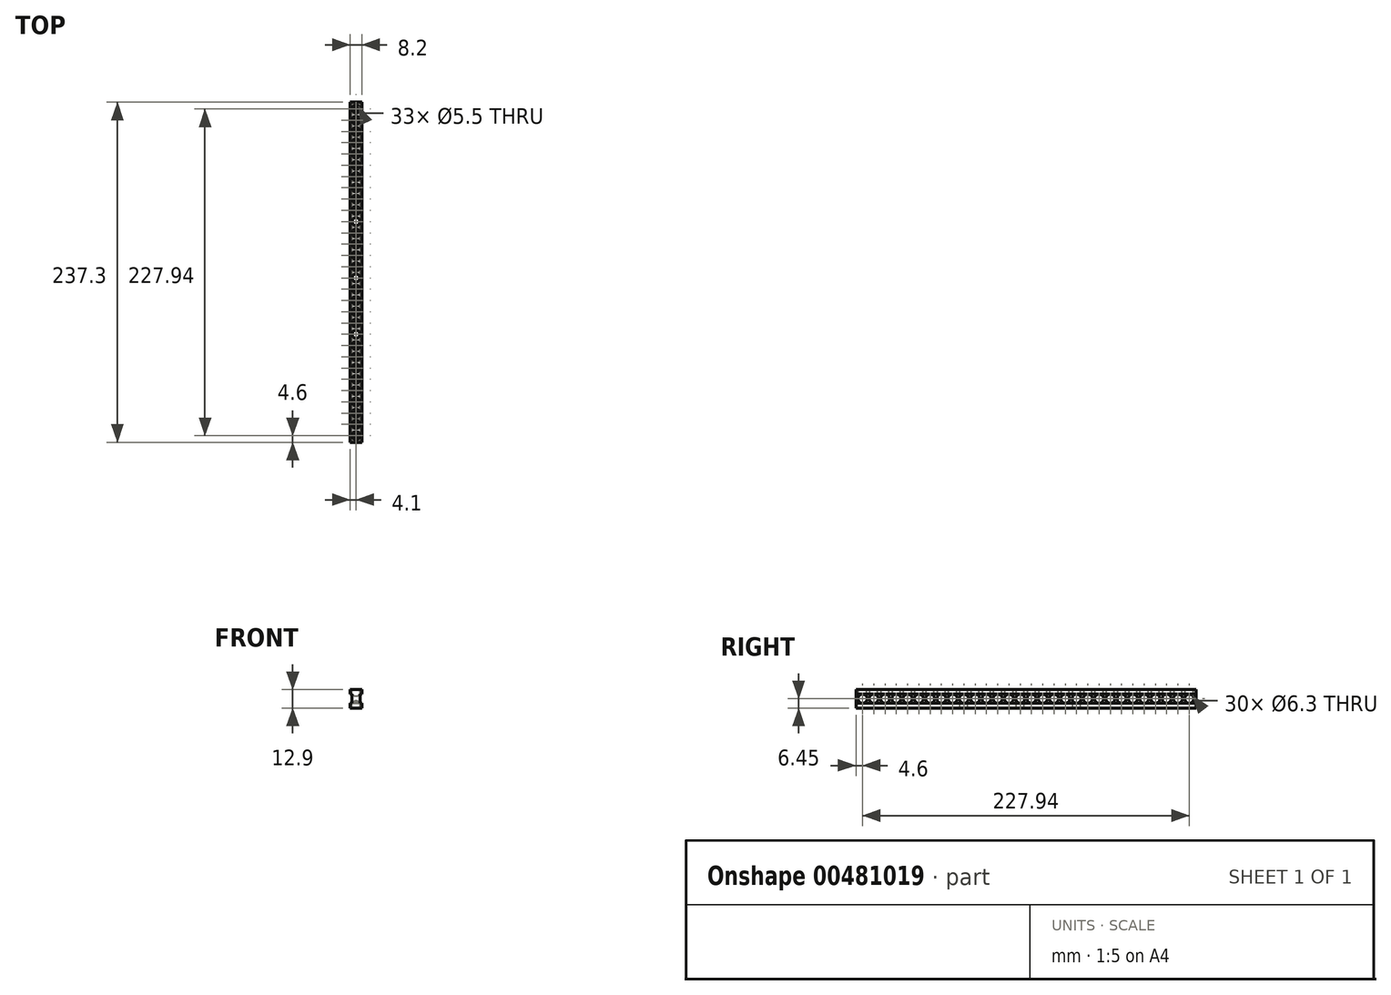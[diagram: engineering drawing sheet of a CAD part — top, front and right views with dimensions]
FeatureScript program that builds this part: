
annotation { "Feature Type Name" : "Feature", "Feature Type Description" : "" }
export const myFeature = defineFeature(function(context is Context, id is Id, definition is map)
    precondition{}
    {
        {
            var Q0;
            Q0=qCreatedBy(makeId("Front.planeOp"),FACE);
            var sketch = newSketch(context, id + "F0", { "sketchPlane" : qUnion([Q0])});
            skLineSegment(sketch, "E0", {"start": v(0, 0) * mm, "end": v(8.2, 0) * mm});
            skLineSegment(sketch, "E1", {"start": v(8.2, 0) * mm, "end": v(8.2, 3.25) * mm});
            skLineSegment(sketch, "E2", {"start": v(8.2, 3.25) * mm, "end": v(6.9, 3.25) * mm});
            skLineSegment(sketch, "E3", {"start": v(6.9, 3.25) * mm, "end": v(6.9, 9.65) * mm});
            skLineSegment(sketch, "E4", {"start": v(6.9, 9.65) * mm, "end": v(8.2, 9.65) * mm});
            skLineSegment(sketch, "E5", {"start": v(8.2, 9.65) * mm, "end": v(8.2, 12.9) * mm});
            skLineSegment(sketch, "E6", {"start": v(8.2, 12.9) * mm, "end": v(0, 12.9) * mm});
            skLineSegment(sketch, "E7", {"start": v(0, 12.9) * mm, "end": v(0, 9.65) * mm});
            skLineSegment(sketch, "E8", {"start": v(0, 9.65) * mm, "end": v(1.3, 9.65) * mm});
            skLineSegment(sketch, "E9", {"start": v(1.3, 9.65) * mm, "end": v(1.3, 3.25) * mm});
            skLineSegment(sketch, "E10", {"start": v(1.3, 3.25) * mm, "end": v(0, 3.25) * mm});
            skLineSegment(sketch, "E11", {"start": v(0, 3.25) * mm, "end": v(0, 0) * mm});
            skSolve(sketch);
        }
        {
            var Q0;
            Q0=makeQuery(id+"F0.imprint","IMPRINT",FACE,{"disambiguationData":[TD([[makeQuery(id+"F0.imprint","IMPRINT",EDGE,{"derivedFrom":sQuery(id+"F0.wireOp",EDGE,"E0")}),1.0]])]});
            extrude(context, id + "F1", {"entities" : qUnion([Q0]), "depth" : 237.3 * mm});
        }
        {
            var Q0;
            Q0=makeQuery(id+"F1.opExtrude","SWEPT_FACE",FACE,{"disambiguationData":[OSD([sQuery(id+"F0.wireOp",EDGE,"E3")])]});
            var sketch = newSketch(context, id + "F2", { "sketchPlane" : qUnion([Q0])});
            skCircle(sketch, "E12", {"center": v(-232.7, 6.45) * mm, "radius": 3.15 * mm});
            skPoint(sketch, "E12.centerSnap0", {"position": v(-237.3, 6.45) * mm});
            skLineSegment(sketch, "E13.direction1", {"start": v(-232.7, 6.45) * mm, "end": v(-224.84, 6.45) * mm, "construction": true});
            skCircle(sketch, "E14.0.1.0", {"center": v(-224.84, 6.45) * mm, "radius": 3.15 * mm});
            skCircle(sketch, "E15.0.2.0", {"center": v(-216.98, 6.45) * mm, "radius": 3.15 * mm});
            skCircle(sketch, "E15.0.3.0", {"center": v(-209.12, 6.45) * mm, "radius": 3.15 * mm});
            skCircle(sketch, "E15.0.4.0", {"center": v(-201.26, 6.45) * mm, "radius": 3.15 * mm});
            skCircle(sketch, "E15.0.5.0", {"center": v(-193.4, 6.45) * mm, "radius": 3.15 * mm});
            skCircle(sketch, "E15.0.6.0", {"center": v(-185.54, 6.45) * mm, "radius": 3.15 * mm});
            skCircle(sketch, "E15.0.7.0", {"center": v(-177.68, 6.45) * mm, "radius": 3.15 * mm});
            skCircle(sketch, "E15.0.8.0", {"center": v(-169.82, 6.45) * mm, "radius": 3.15 * mm});
            skCircle(sketch, "E15.0.9.0", {"center": v(-161.96, 6.45) * mm, "radius": 3.15 * mm});
            skCircle(sketch, "E15.0.10.0", {"center": v(-154.1, 6.45) * mm, "radius": 3.15 * mm});
            skCircle(sketch, "E15.0.11.0", {"center": v(-146.24, 6.45) * mm, "radius": 3.15 * mm});
            skCircle(sketch, "E15.0.12.0", {"center": v(-138.38, 6.45) * mm, "radius": 3.15 * mm});
            skCircle(sketch, "E15.0.13.0", {"center": v(-130.52, 6.45) * mm, "radius": 3.15 * mm});
            skCircle(sketch, "E15.0.14.0", {"center": v(-122.66, 6.45) * mm, "radius": 3.15 * mm});
            skCircle(sketch, "E15.0.15.0", {"center": v(-114.8, 6.45) * mm, "radius": 3.15 * mm});
            skCircle(sketch, "E15.0.16.0", {"center": v(-106.94, 6.45) * mm, "radius": 3.15 * mm});
            skCircle(sketch, "E15.0.17.0", {"center": v(-99.08, 6.45) * mm, "radius": 3.15 * mm});
            skCircle(sketch, "E15.0.18.0", {"center": v(-91.22, 6.45) * mm, "radius": 3.15 * mm});
            skCircle(sketch, "E15.0.19.0", {"center": v(-83.36, 6.45) * mm, "radius": 3.15 * mm});
            skCircle(sketch, "E15.0.20.0", {"center": v(-75.5, 6.45) * mm, "radius": 3.15 * mm});
            skCircle(sketch, "E15.0.21.0", {"center": v(-67.64, 6.45) * mm, "radius": 3.15 * mm});
            skCircle(sketch, "E15.0.22.0", {"center": v(-59.78, 6.45) * mm, "radius": 3.15 * mm});
            skCircle(sketch, "E15.0.23.0", {"center": v(-51.92, 6.45) * mm, "radius": 3.15 * mm});
            skCircle(sketch, "E15.0.24.0", {"center": v(-44.06, 6.45) * mm, "radius": 3.15 * mm});
            skCircle(sketch, "E15.0.25.0", {"center": v(-36.2, 6.45) * mm, "radius": 3.15 * mm});
            skCircle(sketch, "E15.0.26.0", {"center": v(-28.34, 6.45) * mm, "radius": 3.15 * mm});
            skCircle(sketch, "E15.0.27.0", {"center": v(-20.48, 6.45) * mm, "radius": 3.15 * mm});
            skCircle(sketch, "E15.0.28.0", {"center": v(-12.62, 6.45) * mm, "radius": 3.15 * mm});
            skCircle(sketch, "E15.0.29.0", {"center": v(-4.76, 6.45) * mm, "radius": 3.15 * mm});
            skSolve(sketch);
        }
        {
            var Q0;
            Q0=makeQuery(id+"F2.imprint","IMPRINT",FACE,{"disambiguationData":[TD([[makeQuery(id+"F2.imprint","IMPRINT",EDGE,{"derivedFrom":sQuery(id+"F2.wireOp",EDGE,"E12")}),1.0]])]});
            var Q1;
            Q1=makeQuery(id+"F2.imprint","IMPRINT",FACE,{"disambiguationData":[TD([[makeQuery(id+"F2.imprint","IMPRINT",EDGE,{"derivedFrom":sQuery(id+"F2.wireOp",EDGE,"E13.1.0.0")}),1.0]])]});
            var Q2;
            Q2=makeQuery(id+"F2.imprint","IMPRINT",FACE,{"disambiguationData":[TD([[makeQuery(id+"F2.imprint","IMPRINT",EDGE,{"derivedFrom":sQuery(id+"F2.wireOp",EDGE,"E13.2.0.0")}),1.0]])]});
            var Q3;
            Q3=makeQuery(id+"F2.imprint","IMPRINT",FACE,{"disambiguationData":[TD([[makeQuery(id+"F2.imprint","IMPRINT",EDGE,{"derivedFrom":sQuery(id+"F2.wireOp",EDGE,"E13.3.0.0")}),1.0]])]});
            var Q4;
            Q4=makeQuery(id+"F2.imprint","IMPRINT",FACE,{"disambiguationData":[TD([[makeQuery(id+"F2.imprint","IMPRINT",EDGE,{"derivedFrom":sQuery(id+"F2.wireOp",EDGE,"E13.4.0.0")}),1.0]])]});
            var Q5;
            Q5=makeQuery(id+"F2.imprint","IMPRINT",FACE,{"disambiguationData":[TD([[makeQuery(id+"F2.imprint","IMPRINT",EDGE,{"derivedFrom":sQuery(id+"F2.wireOp",EDGE,"E13.5.0.0")}),1.0]])]});
            var Q6;
            Q6=makeQuery(id+"F2.imprint","IMPRINT",FACE,{"disambiguationData":[TD([[makeQuery(id+"F2.imprint","IMPRINT",EDGE,{"derivedFrom":sQuery(id+"F2.wireOp",EDGE,"E13.6.0.0")}),1.0]])]});
            var Q7;
            Q7=makeQuery(id+"F2.imprint","IMPRINT",FACE,{"disambiguationData":[TD([[makeQuery(id+"F2.imprint","IMPRINT",EDGE,{"derivedFrom":sQuery(id+"F2.wireOp",EDGE,"E13.7.0.0")}),1.0]])]});
            var Q8;
            Q8=makeQuery(id+"F2.imprint","IMPRINT",FACE,{"disambiguationData":[TD([[makeQuery(id+"F2.imprint","IMPRINT",EDGE,{"derivedFrom":sQuery(id+"F2.wireOp",EDGE,"E13.8.0.0")}),1.0]])]});
            var Q9;
            Q9=makeQuery(id+"F2.imprint","IMPRINT",FACE,{"disambiguationData":[TD([[makeQuery(id+"F2.imprint","IMPRINT",EDGE,{"derivedFrom":sQuery(id+"F2.wireOp",EDGE,"E13.9.0.0")}),1.0]])]});
            var Q10;
            Q10=makeQuery(id+"F2.imprint","IMPRINT",FACE,{"disambiguationData":[TD([[makeQuery(id+"F2.imprint","IMPRINT",EDGE,{"derivedFrom":sQuery(id+"F2.wireOp",EDGE,"E13.10.0.0")}),1.0]])]});
            var Q11;
            Q11=makeQuery(id+"F2.imprint","IMPRINT",FACE,{"disambiguationData":[TD([[makeQuery(id+"F2.imprint","IMPRINT",EDGE,{"derivedFrom":sQuery(id+"F2.wireOp",EDGE,"E13.11.0.0")}),1.0]])]});
            var Q12;
            Q12=makeQuery(id+"F2.imprint","IMPRINT",FACE,{"disambiguationData":[TD([[makeQuery(id+"F2.imprint","IMPRINT",EDGE,{"derivedFrom":sQuery(id+"F2.wireOp",EDGE,"E13.12.0.0")}),1.0]])]});
            var Q13;
            Q13=makeQuery(id+"F2.imprint","IMPRINT",FACE,{"disambiguationData":[TD([[makeQuery(id+"F2.imprint","IMPRINT",EDGE,{"derivedFrom":sQuery(id+"F2.wireOp",EDGE,"E13.13.0.0")}),1.0]])]});
            var Q14;
            Q14=makeQuery(id+"F2.imprint","IMPRINT",FACE,{"disambiguationData":[TD([[makeQuery(id+"F2.imprint","IMPRINT",EDGE,{"derivedFrom":sQuery(id+"F2.wireOp",EDGE,"E13.14.0.0")}),1.0]])]});
            var Q15;
            Q15=makeQuery(id+"F2.imprint","IMPRINT",FACE,{"disambiguationData":[TD([[makeQuery(id+"F2.imprint","IMPRINT",EDGE,{"derivedFrom":sQuery(id+"F2.wireOp",EDGE,"E13.15.0.0")}),1.0]])]});
            var Q16;
            Q16=makeQuery(id+"F2.imprint","IMPRINT",FACE,{"disambiguationData":[TD([[makeQuery(id+"F2.imprint","IMPRINT",EDGE,{"derivedFrom":sQuery(id+"F2.wireOp",EDGE,"E13.16.0.0")}),1.0]])]});
            var Q17;
            Q17=makeQuery(id+"F2.imprint","IMPRINT",FACE,{"disambiguationData":[TD([[makeQuery(id+"F2.imprint","IMPRINT",EDGE,{"derivedFrom":sQuery(id+"F2.wireOp",EDGE,"E13.17.0.0")}),1.0]])]});
            var Q18;
            Q18=makeQuery(id+"F2.imprint","IMPRINT",FACE,{"disambiguationData":[TD([[makeQuery(id+"F2.imprint","IMPRINT",EDGE,{"derivedFrom":sQuery(id+"F2.wireOp",EDGE,"E13.18.0.0")}),1.0]])]});
            var Q19;
            Q19=makeQuery(id+"F2.imprint","IMPRINT",FACE,{"disambiguationData":[TD([[makeQuery(id+"F2.imprint","IMPRINT",EDGE,{"derivedFrom":sQuery(id+"F2.wireOp",EDGE,"E13.19.0.0")}),1.0]])]});
            var Q20;
            Q20=makeQuery(id+"F2.imprint","IMPRINT",FACE,{"disambiguationData":[TD([[makeQuery(id+"F2.imprint","IMPRINT",EDGE,{"derivedFrom":sQuery(id+"F2.wireOp",EDGE,"E13.20.0.0")}),1.0]])]});
            var Q21;
            Q21=makeQuery(id+"F2.imprint","IMPRINT",FACE,{"disambiguationData":[TD([[makeQuery(id+"F2.imprint","IMPRINT",EDGE,{"derivedFrom":sQuery(id+"F2.wireOp",EDGE,"E13.21.0.0")}),1.0]])]});
            var Q22;
            Q22=makeQuery(id+"F2.imprint","IMPRINT",FACE,{"disambiguationData":[TD([[makeQuery(id+"F2.imprint","IMPRINT",EDGE,{"derivedFrom":sQuery(id+"F2.wireOp",EDGE,"E13.22.0.0")}),1.0]])]});
            var Q23;
            Q23=makeQuery(id+"F2.imprint","IMPRINT",FACE,{"disambiguationData":[TD([[makeQuery(id+"F2.imprint","IMPRINT",EDGE,{"derivedFrom":sQuery(id+"F2.wireOp",EDGE,"E13.23.0.0")}),1.0]])]});
            var Q24;
            Q24=makeQuery(id+"F2.imprint","IMPRINT",FACE,{"disambiguationData":[TD([[makeQuery(id+"F2.imprint","IMPRINT",EDGE,{"derivedFrom":sQuery(id+"F2.wireOp",EDGE,"E13.24.0.0")}),1.0]])]});
            var Q25;
            Q25=makeQuery(id+"F2.imprint","IMPRINT",FACE,{"disambiguationData":[TD([[makeQuery(id+"F2.imprint","IMPRINT",EDGE,{"derivedFrom":sQuery(id+"F2.wireOp",EDGE,"E13.25.0.0")}),1.0]])]});
            var Q26;
            Q26=makeQuery(id+"F2.imprint","IMPRINT",FACE,{"disambiguationData":[TD([[makeQuery(id+"F2.imprint","IMPRINT",EDGE,{"derivedFrom":sQuery(id+"F2.wireOp",EDGE,"E13.26.0.0")}),1.0]])]});
            var Q27;
            Q27=makeQuery(id+"F2.imprint","IMPRINT",FACE,{"disambiguationData":[TD([[makeQuery(id+"F2.imprint","IMPRINT",EDGE,{"derivedFrom":sQuery(id+"F2.wireOp",EDGE,"E13.27.0.0")}),1.0]])]});
            var Q28;
            Q28=makeQuery(id+"F2.imprint","IMPRINT",FACE,{"disambiguationData":[TD([[makeQuery(id+"F2.imprint","IMPRINT",EDGE,{"derivedFrom":sQuery(id+"F2.wireOp",EDGE,"E13.28.0.0")}),1.0]])]});
            var Q29;
            Q29=makeQuery(id+"F2.imprint","IMPRINT",FACE,{"disambiguationData":[TD([[makeQuery(id+"F2.imprint","IMPRINT",EDGE,{"derivedFrom":sQuery(id+"F2.wireOp",EDGE,"E14.0.1.0")}),1.0]])]});
            var Q30;
            Q30=makeQuery(id+"F2.imprint","IMPRINT",FACE,{"disambiguationData":[TD([[makeQuery(id+"F2.imprint","IMPRINT",EDGE,{"derivedFrom":sQuery(id+"F2.wireOp",EDGE,"E15.0.2.0")}),1.0]])]});
            var Q31;
            Q31=makeQuery(id+"F2.imprint","IMPRINT",FACE,{"disambiguationData":[TD([[makeQuery(id+"F2.imprint","IMPRINT",EDGE,{"derivedFrom":sQuery(id+"F2.wireOp",EDGE,"E15.0.3.0")}),1.0]])]});
            var Q32;
            Q32=makeQuery(id+"F2.imprint","IMPRINT",FACE,{"disambiguationData":[TD([[makeQuery(id+"F2.imprint","IMPRINT",EDGE,{"derivedFrom":sQuery(id+"F2.wireOp",EDGE,"E15.0.4.0")}),1.0]])]});
            var Q33;
            Q33=makeQuery(id+"F2.imprint","IMPRINT",FACE,{"disambiguationData":[TD([[makeQuery(id+"F2.imprint","IMPRINT",EDGE,{"derivedFrom":sQuery(id+"F2.wireOp",EDGE,"E15.0.5.0")}),1.0]])]});
            var Q34;
            Q34=makeQuery(id+"F2.imprint","IMPRINT",FACE,{"disambiguationData":[TD([[makeQuery(id+"F2.imprint","IMPRINT",EDGE,{"derivedFrom":sQuery(id+"F2.wireOp",EDGE,"E15.0.6.0")}),1.0]])]});
            var Q35;
            Q35=makeQuery(id+"F2.imprint","IMPRINT",FACE,{"disambiguationData":[TD([[makeQuery(id+"F2.imprint","IMPRINT",EDGE,{"derivedFrom":sQuery(id+"F2.wireOp",EDGE,"E15.0.7.0")}),1.0]])]});
            var Q36;
            Q36=makeQuery(id+"F2.imprint","IMPRINT",FACE,{"disambiguationData":[TD([[makeQuery(id+"F2.imprint","IMPRINT",EDGE,{"derivedFrom":sQuery(id+"F2.wireOp",EDGE,"E15.0.8.0")}),1.0]])]});
            var Q37;
            Q37=makeQuery(id+"F2.imprint","IMPRINT",FACE,{"disambiguationData":[TD([[makeQuery(id+"F2.imprint","IMPRINT",EDGE,{"derivedFrom":sQuery(id+"F2.wireOp",EDGE,"E15.0.9.0")}),1.0]])]});
            var Q38;
            Q38=makeQuery(id+"F2.imprint","IMPRINT",FACE,{"disambiguationData":[TD([[makeQuery(id+"F2.imprint","IMPRINT",EDGE,{"derivedFrom":sQuery(id+"F2.wireOp",EDGE,"E15.0.10.0")}),1.0]])]});
            var Q39;
            Q39=makeQuery(id+"F2.imprint","IMPRINT",FACE,{"disambiguationData":[TD([[makeQuery(id+"F2.imprint","IMPRINT",EDGE,{"derivedFrom":sQuery(id+"F2.wireOp",EDGE,"E15.0.11.0")}),1.0]])]});
            var Q40;
            Q40=makeQuery(id+"F2.imprint","IMPRINT",FACE,{"disambiguationData":[TD([[makeQuery(id+"F2.imprint","IMPRINT",EDGE,{"derivedFrom":sQuery(id+"F2.wireOp",EDGE,"E15.0.12.0")}),1.0]])]});
            var Q41;
            Q41=makeQuery(id+"F2.imprint","IMPRINT",FACE,{"disambiguationData":[TD([[makeQuery(id+"F2.imprint","IMPRINT",EDGE,{"derivedFrom":sQuery(id+"F2.wireOp",EDGE,"E15.0.13.0")}),1.0]])]});
            var Q42;
            Q42=makeQuery(id+"F2.imprint","IMPRINT",FACE,{"disambiguationData":[TD([[makeQuery(id+"F2.imprint","IMPRINT",EDGE,{"derivedFrom":sQuery(id+"F2.wireOp",EDGE,"E15.0.14.0")}),1.0]])]});
            var Q43;
            Q43=makeQuery(id+"F2.imprint","IMPRINT",FACE,{"disambiguationData":[TD([[makeQuery(id+"F2.imprint","IMPRINT",EDGE,{"derivedFrom":sQuery(id+"F2.wireOp",EDGE,"E15.0.15.0")}),1.0]])]});
            var Q44;
            Q44=makeQuery(id+"F2.imprint","IMPRINT",FACE,{"disambiguationData":[TD([[makeQuery(id+"F2.imprint","IMPRINT",EDGE,{"derivedFrom":sQuery(id+"F2.wireOp",EDGE,"E15.0.16.0")}),1.0]])]});
            var Q45;
            Q45=makeQuery(id+"F2.imprint","IMPRINT",FACE,{"disambiguationData":[TD([[makeQuery(id+"F2.imprint","IMPRINT",EDGE,{"derivedFrom":sQuery(id+"F2.wireOp",EDGE,"E15.0.17.0")}),1.0]])]});
            var Q46;
            Q46=makeQuery(id+"F2.imprint","IMPRINT",FACE,{"disambiguationData":[TD([[makeQuery(id+"F2.imprint","IMPRINT",EDGE,{"derivedFrom":sQuery(id+"F2.wireOp",EDGE,"E15.0.18.0")}),1.0]])]});
            var Q47;
            Q47=makeQuery(id+"F2.imprint","IMPRINT",FACE,{"disambiguationData":[TD([[makeQuery(id+"F2.imprint","IMPRINT",EDGE,{"derivedFrom":sQuery(id+"F2.wireOp",EDGE,"E15.0.19.0")}),1.0]])]});
            var Q48;
            Q48=makeQuery(id+"F2.imprint","IMPRINT",FACE,{"disambiguationData":[TD([[makeQuery(id+"F2.imprint","IMPRINT",EDGE,{"derivedFrom":sQuery(id+"F2.wireOp",EDGE,"E15.0.20.0")}),1.0]])]});
            var Q49;
            Q49=makeQuery(id+"F2.imprint","IMPRINT",FACE,{"disambiguationData":[TD([[makeQuery(id+"F2.imprint","IMPRINT",EDGE,{"derivedFrom":sQuery(id+"F2.wireOp",EDGE,"E15.0.21.0")}),1.0]])]});
            var Q50;
            Q50=makeQuery(id+"F2.imprint","IMPRINT",FACE,{"disambiguationData":[TD([[makeQuery(id+"F2.imprint","IMPRINT",EDGE,{"derivedFrom":sQuery(id+"F2.wireOp",EDGE,"E15.0.22.0")}),1.0]])]});
            var Q51;
            Q51=makeQuery(id+"F2.imprint","IMPRINT",FACE,{"disambiguationData":[TD([[makeQuery(id+"F2.imprint","IMPRINT",EDGE,{"derivedFrom":sQuery(id+"F2.wireOp",EDGE,"E15.0.23.0")}),1.0]])]});
            var Q52;
            Q52=makeQuery(id+"F2.imprint","IMPRINT",FACE,{"disambiguationData":[TD([[makeQuery(id+"F2.imprint","IMPRINT",EDGE,{"derivedFrom":sQuery(id+"F2.wireOp",EDGE,"E15.0.24.0")}),1.0]])]});
            var Q53;
            Q53=makeQuery(id+"F2.imprint","IMPRINT",FACE,{"disambiguationData":[TD([[makeQuery(id+"F2.imprint","IMPRINT",EDGE,{"derivedFrom":sQuery(id+"F2.wireOp",EDGE,"E15.0.25.0")}),1.0]])]});
            var Q54;
            Q54=makeQuery(id+"F2.imprint","IMPRINT",FACE,{"disambiguationData":[TD([[makeQuery(id+"F2.imprint","IMPRINT",EDGE,{"derivedFrom":sQuery(id+"F2.wireOp",EDGE,"E15.0.26.0")}),1.0]])]});
            var Q55;
            Q55=makeQuery(id+"F2.imprint","IMPRINT",FACE,{"disambiguationData":[TD([[makeQuery(id+"F2.imprint","IMPRINT",EDGE,{"derivedFrom":sQuery(id+"F2.wireOp",EDGE,"E15.0.27.0")}),1.0]])]});
            var Q56;
            Q56=makeQuery(id+"F2.imprint","IMPRINT",FACE,{"disambiguationData":[TD([[makeQuery(id+"F2.imprint","IMPRINT",EDGE,{"derivedFrom":sQuery(id+"F2.wireOp",EDGE,"E15.0.28.0")}),1.0]])]});
            var Q57;
            Q57=makeQuery(id+"F2.imprint","IMPRINT",FACE,{"disambiguationData":[TD([[makeQuery(id+"F2.imprint","IMPRINT",EDGE,{"derivedFrom":sQuery(id+"F2.wireOp",EDGE,"E15.0.29.0")}),1.0]])]});
            var Q58;
            Q58=sQuery(id+"F2.wireOp",EDGE,"E12");
            extrude(context, id + "F3", {"entities" : qUnion([Q0, Q1, Q2, Q3, Q4, Q5, Q6, Q7, Q8, Q9, Q10, Q11, Q12, Q13, Q14, Q15, Q16, Q17, Q18, Q19, Q20, Q21, Q22, Q23, Q24, Q25, Q26, Q27, Q28, Q29, Q30, Q31, Q32, Q33, Q34, Q35, Q36, Q37, Q38, Q39, Q40, Q41, Q42, Q43, Q44, Q45, Q46, Q47, Q48, Q49, Q50, Q51, Q52, Q53, Q54, Q55, Q56, Q57]), "operationType" : NewBodyOperationType.REMOVE, "surfaceEntities" : qUnion([Q58]), "endBound" : BoundingType.THROUGH_ALL, "oppositeDirection" : true, "depth" : 25 * mm});
        }
        {
            var Q0;
            Q0=makeQuery(id+"F1.opExtrude","SWEPT_FACE",FACE,{"disambiguationData":[OSD([sQuery(id+"F0.wireOp",EDGE,"E6")])]});
            var sketch = newSketch(context, id + "F4", { "sketchPlane" : qUnion([Q0])});
            skCircle(sketch, "E16", {"center": v(4.1, -232.7) * mm, "radius": 2.75 * mm});
            skPoint(sketch, "E16.centerSnap0", {"position": v(4.1, -237.3) * mm});
            skCircle(sketch, "E17.0.1.0", {"center": v(4.1, -224.84) * mm, "radius": 2.75 * mm});
            skCircle(sketch, "E17.0.2.0", {"center": v(4.1, -216.98) * mm, "radius": 2.75 * mm});
            skCircle(sketch, "E17.0.3.0", {"center": v(4.1, -209.12) * mm, "radius": 2.75 * mm});
            skCircle(sketch, "E17.0.4.0", {"center": v(4.1, -201.26) * mm, "radius": 2.75 * mm});
            skCircle(sketch, "E17.0.5.0", {"center": v(4.1, -193.4) * mm, "radius": 2.75 * mm});
            skCircle(sketch, "E17.0.6.0", {"center": v(4.1, -185.54) * mm, "radius": 2.75 * mm});
            skCircle(sketch, "E17.0.7.0", {"center": v(4.1, -177.68) * mm, "radius": 2.75 * mm});
            skCircle(sketch, "E17.0.8.0", {"center": v(4.1, -169.82) * mm, "radius": 2.75 * mm});
            skCircle(sketch, "E17.0.9.0", {"center": v(4.1, -161.96) * mm, "radius": 2.75 * mm});
            skCircle(sketch, "E17.0.10.0", {"center": v(4.1, -154.1) * mm, "radius": 2.75 * mm});
            skCircle(sketch, "E17.0.11.0", {"center": v(4.1, -146.24) * mm, "radius": 2.75 * mm});
            skCircle(sketch, "E17.0.12.0", {"center": v(4.1, -138.38) * mm, "radius": 2.75 * mm});
            skCircle(sketch, "E17.0.13.0", {"center": v(4.1, -130.52) * mm, "radius": 2.75 * mm});
            skCircle(sketch, "E17.0.14.0", {"center": v(4.1, -122.66) * mm, "radius": 2.75 * mm});
            skCircle(sketch, "E17.0.15.0", {"center": v(4.1, -114.8) * mm, "radius": 2.75 * mm});
            skCircle(sketch, "E17.0.16.0", {"center": v(4.1, -106.94) * mm, "radius": 2.75 * mm});
            skCircle(sketch, "E17.0.17.0", {"center": v(4.1, -99.08) * mm, "radius": 2.75 * mm});
            skCircle(sketch, "E17.0.18.0", {"center": v(4.1, -91.22) * mm, "radius": 2.75 * mm});
            skCircle(sketch, "E17.0.19.0", {"center": v(4.1, -83.36) * mm, "radius": 2.75 * mm});
            skCircle(sketch, "E17.0.20.0", {"center": v(4.1, -75.5) * mm, "radius": 2.75 * mm});
            skCircle(sketch, "E17.0.21.0", {"center": v(4.1, -67.64) * mm, "radius": 2.75 * mm});
            skCircle(sketch, "E17.0.22.0", {"center": v(4.1, -59.78) * mm, "radius": 2.75 * mm});
            skCircle(sketch, "E17.0.23.0", {"center": v(4.1, -51.92) * mm, "radius": 2.75 * mm});
            skCircle(sketch, "E17.0.24.0", {"center": v(4.1, -44.06) * mm, "radius": 2.75 * mm});
            skCircle(sketch, "E17.0.25.0", {"center": v(4.1, -36.2) * mm, "radius": 2.75 * mm});
            skCircle(sketch, "E17.0.26.0", {"center": v(4.1, -28.34) * mm, "radius": 2.75 * mm});
            skCircle(sketch, "E17.0.27.0", {"center": v(4.1, -20.48) * mm, "radius": 2.75 * mm});
            skCircle(sketch, "E17.0.28.0", {"center": v(4.1, -12.62) * mm, "radius": 2.75 * mm});
            skLineSegment(sketch, "E17.direction1", {"start": v(4.1, -232.7) * mm, "end": v(29.1, -232.7) * mm, "construction": true});
            skLineSegment(sketch, "E17.direction2", {"start": v(4.1, -232.7) * mm, "end": v(4.1, -224.84) * mm, "construction": true});
            skCircle(sketch, "E18.0.0.29", {"center": v(4.1, -4.76) * mm, "radius": 2.75 * mm});
            skSolve(sketch);
        }
        {
            var Q0;
            Q0=makeQuery(id+"F4.imprint","IMPRINT",FACE,{"disambiguationData":[TD([[makeQuery(id+"F4.imprint","IMPRINT",EDGE,{"derivedFrom":sQuery(id+"F4.wireOp",EDGE,"E16")}),1.0]])]});
            var Q1;
            Q1=makeQuery(id+"F4.imprint","IMPRINT",FACE,{"disambiguationData":[TD([[makeQuery(id+"F4.imprint","IMPRINT",EDGE,{"derivedFrom":sQuery(id+"F4.wireOp",EDGE,"E17.0.1.0")}),1.0]])]});
            var Q2;
            Q2=makeQuery(id+"F4.imprint","IMPRINT",FACE,{"disambiguationData":[TD([[makeQuery(id+"F4.imprint","IMPRINT",EDGE,{"derivedFrom":sQuery(id+"F4.wireOp",EDGE,"E17.0.2.0")}),1.0]])]});
            var Q3;
            Q3=makeQuery(id+"F4.imprint","IMPRINT",FACE,{"disambiguationData":[TD([[makeQuery(id+"F4.imprint","IMPRINT",EDGE,{"derivedFrom":sQuery(id+"F4.wireOp",EDGE,"E17.0.3.0")}),1.0]])]});
            var Q4;
            Q4=makeQuery(id+"F4.imprint","IMPRINT",FACE,{"disambiguationData":[TD([[makeQuery(id+"F4.imprint","IMPRINT",EDGE,{"derivedFrom":sQuery(id+"F4.wireOp",EDGE,"E17.0.4.0")}),1.0]])]});
            var Q5;
            Q5=makeQuery(id+"F4.imprint","IMPRINT",FACE,{"disambiguationData":[TD([[makeQuery(id+"F4.imprint","IMPRINT",EDGE,{"derivedFrom":sQuery(id+"F4.wireOp",EDGE,"E17.0.5.0")}),1.0]])]});
            var Q6;
            Q6=makeQuery(id+"F4.imprint","IMPRINT",FACE,{"disambiguationData":[TD([[makeQuery(id+"F4.imprint","IMPRINT",EDGE,{"derivedFrom":sQuery(id+"F4.wireOp",EDGE,"E17.0.6.0")}),1.0]])]});
            var Q7;
            Q7=makeQuery(id+"F4.imprint","IMPRINT",FACE,{"disambiguationData":[TD([[makeQuery(id+"F4.imprint","IMPRINT",EDGE,{"derivedFrom":sQuery(id+"F4.wireOp",EDGE,"E17.0.7.0")}),1.0]])]});
            var Q8;
            Q8=makeQuery(id+"F4.imprint","IMPRINT",FACE,{"disambiguationData":[TD([[makeQuery(id+"F4.imprint","IMPRINT",EDGE,{"derivedFrom":sQuery(id+"F4.wireOp",EDGE,"E17.0.8.0")}),1.0]])]});
            var Q9;
            Q9=makeQuery(id+"F4.imprint","IMPRINT",FACE,{"disambiguationData":[TD([[makeQuery(id+"F4.imprint","IMPRINT",EDGE,{"derivedFrom":sQuery(id+"F4.wireOp",EDGE,"E17.0.10.0")}),1.0]])]});
            var Q10;
            Q10=makeQuery(id+"F4.imprint","IMPRINT",FACE,{"disambiguationData":[TD([[makeQuery(id+"F4.imprint","IMPRINT",EDGE,{"derivedFrom":sQuery(id+"F4.wireOp",EDGE,"E17.0.11.0")}),1.0]])]});
            var Q11;
            Q11=makeQuery(id+"F4.imprint","IMPRINT",FACE,{"disambiguationData":[TD([[makeQuery(id+"F4.imprint","IMPRINT",EDGE,{"derivedFrom":sQuery(id+"F4.wireOp",EDGE,"E17.0.12.0")}),1.0]])]});
            var Q12;
            Q12=makeQuery(id+"F4.imprint","IMPRINT",FACE,{"disambiguationData":[TD([[makeQuery(id+"F4.imprint","IMPRINT",EDGE,{"derivedFrom":sQuery(id+"F4.wireOp",EDGE,"E17.0.13.0")}),1.0]])]});
            var Q13;
            Q13=makeQuery(id+"F4.imprint","IMPRINT",FACE,{"disambiguationData":[TD([[makeQuery(id+"F4.imprint","IMPRINT",EDGE,{"derivedFrom":sQuery(id+"F4.wireOp",EDGE,"E17.0.15.0")}),1.0]])]});
            var Q14;
            Q14=makeQuery(id+"F4.imprint","IMPRINT",FACE,{"disambiguationData":[TD([[makeQuery(id+"F4.imprint","IMPRINT",EDGE,{"derivedFrom":sQuery(id+"F4.wireOp",EDGE,"E17.0.16.0")}),1.0]])]});
            var Q15;
            Q15=makeQuery(id+"F4.imprint","IMPRINT",FACE,{"disambiguationData":[TD([[makeQuery(id+"F4.imprint","IMPRINT",EDGE,{"derivedFrom":sQuery(id+"F4.wireOp",EDGE,"E17.0.17.0")}),1.0]])]});
            var Q16;
            Q16=makeQuery(id+"F4.imprint","IMPRINT",FACE,{"disambiguationData":[TD([[makeQuery(id+"F4.imprint","IMPRINT",EDGE,{"derivedFrom":sQuery(id+"F4.wireOp",EDGE,"E17.0.18.0")}),1.0]])]});
            var Q17;
            Q17=makeQuery(id+"F4.imprint","IMPRINT",FACE,{"disambiguationData":[TD([[makeQuery(id+"F4.imprint","IMPRINT",EDGE,{"derivedFrom":sQuery(id+"F4.wireOp",EDGE,"E17.0.20.0")}),1.0]])]});
            var Q18;
            Q18=makeQuery(id+"F4.imprint","IMPRINT",FACE,{"disambiguationData":[TD([[makeQuery(id+"F4.imprint","IMPRINT",EDGE,{"derivedFrom":sQuery(id+"F4.wireOp",EDGE,"E17.0.21.0")}),1.0]])]});
            var Q19;
            Q19=makeQuery(id+"F4.imprint","IMPRINT",FACE,{"disambiguationData":[TD([[makeQuery(id+"F4.imprint","IMPRINT",EDGE,{"derivedFrom":sQuery(id+"F4.wireOp",EDGE,"E17.0.22.0")}),1.0]])]});
            var Q20;
            Q20=makeQuery(id+"F4.imprint","IMPRINT",FACE,{"disambiguationData":[TD([[makeQuery(id+"F4.imprint","IMPRINT",EDGE,{"derivedFrom":sQuery(id+"F4.wireOp",EDGE,"E17.0.23.0")}),1.0]])]});
            var Q21;
            Q21=makeQuery(id+"F4.imprint","IMPRINT",FACE,{"disambiguationData":[TD([[makeQuery(id+"F4.imprint","IMPRINT",EDGE,{"derivedFrom":sQuery(id+"F4.wireOp",EDGE,"E17.0.24.0")}),1.0]])]});
            var Q22;
            Q22=makeQuery(id+"F4.imprint","IMPRINT",FACE,{"disambiguationData":[TD([[makeQuery(id+"F4.imprint","IMPRINT",EDGE,{"derivedFrom":sQuery(id+"F4.wireOp",EDGE,"E17.0.25.0")}),1.0]])]});
            var Q23;
            Q23=makeQuery(id+"F4.imprint","IMPRINT",FACE,{"disambiguationData":[TD([[makeQuery(id+"F4.imprint","IMPRINT",EDGE,{"derivedFrom":sQuery(id+"F4.wireOp",EDGE,"E17.0.26.0")}),1.0]])]});
            var Q24;
            Q24=makeQuery(id+"F4.imprint","IMPRINT",FACE,{"disambiguationData":[TD([[makeQuery(id+"F4.imprint","IMPRINT",EDGE,{"derivedFrom":sQuery(id+"F4.wireOp",EDGE,"E17.0.27.0")}),1.0]])]});
            var Q25;
            Q25=makeQuery(id+"F4.imprint","IMPRINT",FACE,{"disambiguationData":[TD([[makeQuery(id+"F4.imprint","IMPRINT",EDGE,{"derivedFrom":sQuery(id+"F4.wireOp",EDGE,"E17.0.28.0")}),1.0]])]});
            var Q26;
            Q26=makeQuery(id+"F4.imprint","IMPRINT",FACE,{"disambiguationData":[TD([[makeQuery(id+"F4.imprint","IMPRINT",EDGE,{"derivedFrom":sQuery(id+"F4.wireOp",EDGE,"E18.0.0.29")}),1.0]])]});
            extrude(context, id + "F5", {"entities" : qUnion([Q0, Q1, Q2, Q3, Q4, Q5, Q6, Q7, Q8, Q9, Q10, Q11, Q12, Q13, Q14, Q15, Q16, Q17, Q18, Q19, Q20, Q21, Q22, Q23, Q24, Q25, Q26]), "operationType" : NewBodyOperationType.REMOVE, "oppositeDirection" : true, "depth" : 9.3 * mm});
        }
        {
            var Q0;
            Q0=makeQuery(id+"F4.imprint","IMPRINT",FACE,{"disambiguationData":[TD([[makeQuery(id+"F4.imprint","IMPRINT",EDGE,{"derivedFrom":sQuery(id+"F4.wireOp",EDGE,"E17.0.9.0")}),1.0]])]});
            var Q1;
            Q1=makeQuery(id+"F4.imprint","IMPRINT",FACE,{"disambiguationData":[TD([[makeQuery(id+"F4.imprint","IMPRINT",EDGE,{"derivedFrom":sQuery(id+"F4.wireOp",EDGE,"E17.0.14.0")}),1.0]])]});
            var Q2;
            Q2=makeQuery(id+"F4.imprint","IMPRINT",FACE,{"disambiguationData":[TD([[makeQuery(id+"F4.imprint","IMPRINT",EDGE,{"derivedFrom":sQuery(id+"F4.wireOp",EDGE,"E17.0.19.0")}),1.0]])]});
            extrude(context, id + "F6", {"entities" : qUnion([Q0, Q1, Q2]), "operationType" : NewBodyOperationType.REMOVE, "endBound" : BoundingType.THROUGH_ALL, "oppositeDirection" : true, "depth" : 25 * mm});
        }
    });
